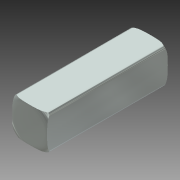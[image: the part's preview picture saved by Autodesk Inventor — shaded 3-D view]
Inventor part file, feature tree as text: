
AUTODESK INVENTOR PART (.ipt)
format: ipt  version: 2013 (Build 170138000, 138)  size: 183,808 bytes
history: native  units: in
note: dims shown in document units (in); Inventor stores cm internally (conversion verified against a paired STEP export)
features: sketch x2, plane x2, extrude x1, revolve x1, mirror x1, other x1
ambient origin geometry x8: Origin, YZ Plane, XZ Plane, XY Plane, X Axis, Y Axis, Z Axis, Center Point
bodies: Solid1 (feature_tree)
feature tree (8):
  sketch  "Sketch1"  dims[d0=0.4331in d1=0.0in d2=90.0deg]
  extrude  "Extrusion1"  TaperAngle=90.0deg  [1 undecoded]
  plane  "Work Plane1"
  revolve  "Revolution1"  [1 undecoded]
  plane  "Work Plane2"
  mirror  "Mirror1"
  other  "Work Axis1"
  sketch  "Sketch2"  dims[d3=90.0deg]
note: 2 required parameter values undecoded (feature->parameter linkage not recoverable at this tier; creation-order binding heuristic only, values carry confidence <= 0.55)
